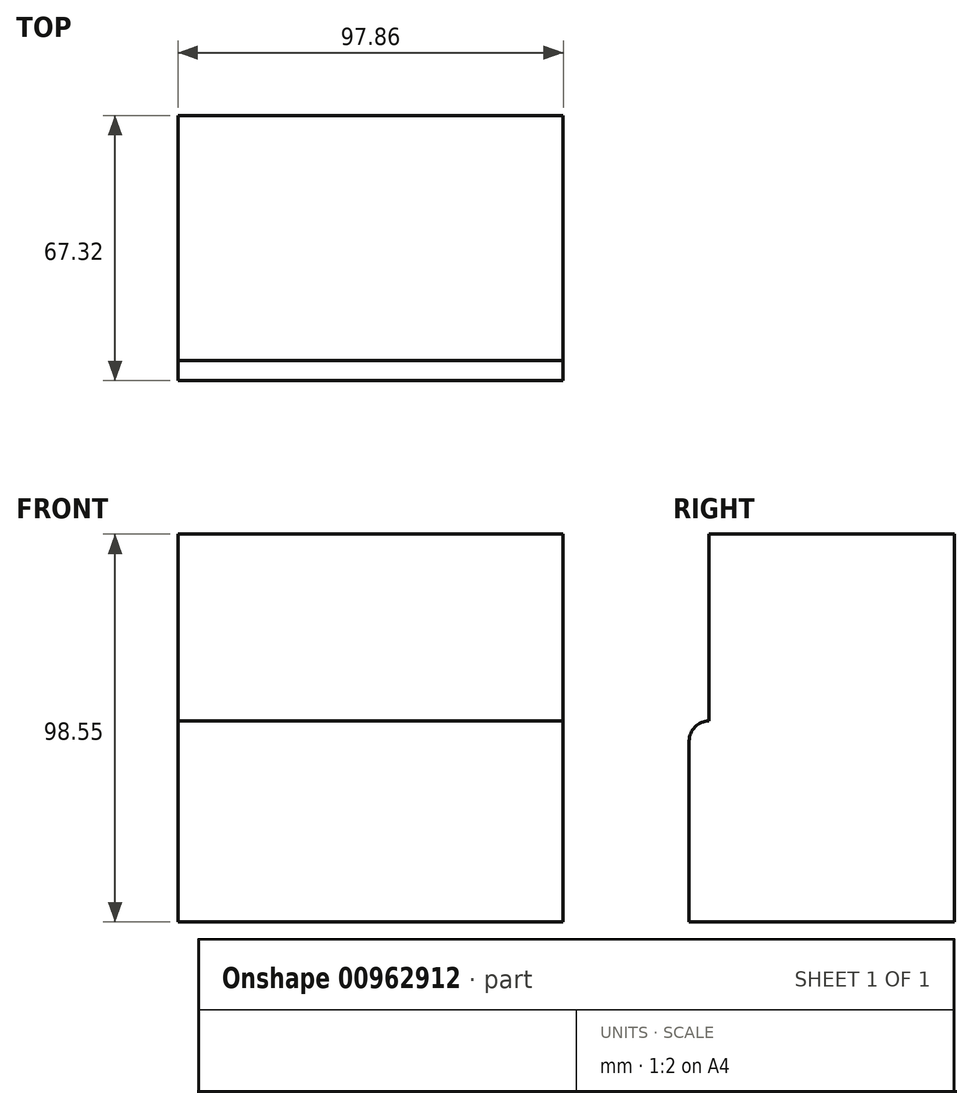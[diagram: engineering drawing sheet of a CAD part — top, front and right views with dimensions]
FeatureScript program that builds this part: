
annotation { "Feature Type Name" : "Feature", "Feature Type Description" : "" }
export const myFeature = defineFeature(function(context is Context, id is Id, definition is map)
    precondition{}
    {
        {
            var Q0;
            Q0=qCreatedBy(makeId("Top.planeOp"),FACE);
            var sketch = newSketch(context, id + "F0", { "sketchPlane" : qUnion([Q0])});
            skLineSegment(sketch, "E0.bottom", {"start": v(-55.24, 34.07) * mm, "end": v(42.62, 34.07) * mm});
            skLineSegment(sketch, "E0.top", {"start": v(-55.24, -33.25) * mm, "end": v(42.62, -33.25) * mm});
            skLineSegment(sketch, "E0.left", {"start": v(-55.24, 34.07) * mm, "end": v(-55.24, -33.25) * mm});
            skLineSegment(sketch, "E0.right", {"start": v(42.62, 34.07) * mm, "end": v(42.62, -33.25) * mm});
            skSolve(sketch);
        }
        {
            var Q0;
            Q0=makeQuery(id+"F0.imprint","IMPRINT",FACE,{"disambiguationData":[TD([[makeQuery(id+"F0.imprint","IMPRINT",EDGE,{"derivedFrom":sQuery(id+"F0.wireOp",EDGE,"E0.bottom")}),-1.0]])]});
            extrude(context, id + "F1", {"entities" : qUnion([Q0]), "depth" : 51.05 * mm, "offsetDistance" : 25.4 * mm});
        }
        {
            var Q0;
            Q0=makeQuery(id+"F1.opExtrude","CAP_EDGE",EDGE,{"disambiguationData":[OSD([sQuery(id+"F0.wireOp",EDGE,"E0.top")])],"isStart":false});
            fillet(context, id + "F2", {"entities" : qUnion([Q0]), "radius" : 5.08 * mm, "tangentPropagation" : true, "allowEdgeOverflow" : false});
        }
        {
            var Q0;
            Q0=makeQuery(id+"F1.opExtrude","CAP_FACE",FACE,{"disambiguationData":[OSD([sQuery(id+"F0.wireOp",EDGE,"E0.bottom"),sQuery(id+"F0.wireOp",EDGE,"E0.top"),sQuery(id+"F0.wireOp",EDGE,"E0.left"),sQuery(id+"F0.wireOp",EDGE,"E0.right")])],"isStart":false});
            extrude(context, id + "F3", {"entities" : qUnion([Q0]), "operationType" : NewBodyOperationType.ADD, "depth" : 47.5 * mm, "offsetDistance" : 25.4 * mm});
        }
    });
